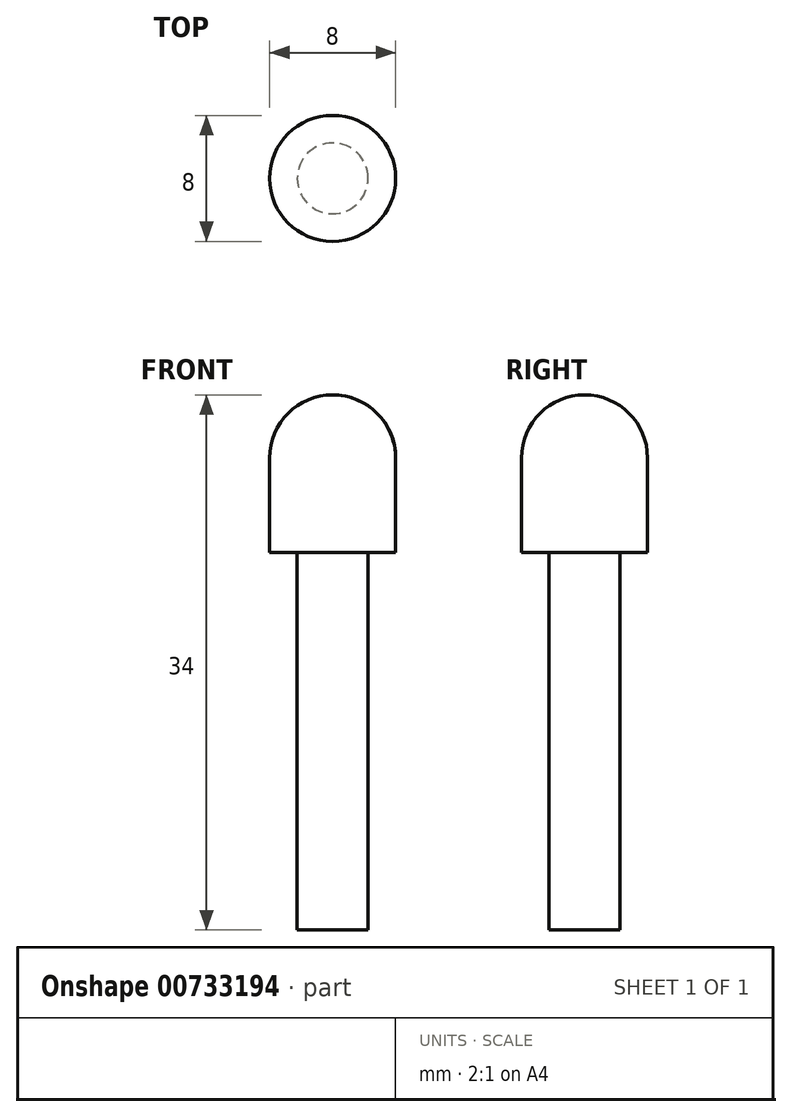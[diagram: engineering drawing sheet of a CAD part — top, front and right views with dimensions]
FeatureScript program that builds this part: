
annotation { "Feature Type Name" : "Feature", "Feature Type Description" : "" }
export const myFeature = defineFeature(function(context is Context, id is Id, definition is map)
    precondition{}
    {
        {
            var Q0;
            Q0=qCreatedBy(makeId("Top.planeOp"),FACE);
            var sketch = newSketch(context, id + "F0", { "sketchPlane" : qUnion([Q0])});
            skCircle(sketch, "E0", {"center": v(0, 0) * mm, "radius": 2.25 * mm});
            skSolve(sketch);
        }
        {
            var Q0;
            Q0=makeQuery(id+"F0.imprint","IMPRINT",FACE,{"disambiguationData":[TD([[makeQuery(id+"F0.imprint","IMPRINT",EDGE,{"derivedFrom":sQuery(id+"F0.wireOp",EDGE,"E0")}),1.0]])]});
            extrude(context, id + "F1", {"entities" : qUnion([Q0]), "depth" : 24 * mm, "offsetDistance" : 25 * mm});
        }
        {
            var Q0;
            Q0=makeQuery(id+"F1.opExtrude","CAP_FACE",FACE,{"disambiguationData":[OSD([sQuery(id+"F0.wireOp",EDGE,"E0")])],"isStart":false});
            var sketch = newSketch(context, id + "F2", { "sketchPlane" : qUnion([Q0])});
            skCircle(sketch, "E1", {"center": v(0, 0) * mm, "radius": 4 * mm});
            skSolve(sketch);
        }
        {
            var Q0;
            Q0=makeQuery(id+"F2.imprint","IMPRINT",FACE,{"disambiguationData":[TD([[makeQuery(id+"F2.imprint","IMPRINT",EDGE,{"derivedFrom":sQuery(id+"F2.wireOp",EDGE,"E1")}),1.0]])]});
            var Q1;
            Q1=makeQuery(id+"F2.imprint","IMPRINT",FACE,{"disambiguationData":[TD([[makeQuery(id+"F2.imprint","IMPRINT",EDGE,{"derivedFrom":makeQuery(id+"F1.opExtrude","CAP_EDGE",EDGE,{"disambiguationData":[OSD([sQuery(id+"F0.wireOp",EDGE,"E0")])],"isStart":false})}),1.0]])]});
            extrude(context, id + "F3", {"entities" : qUnion([Q0, Q1]), "operationType" : NewBodyOperationType.ADD, "depth" : 10 * mm, "offsetDistance" : 25 * mm});
        }
        {
            var Q0;
            Q0=makeQuery(id+"F3.opExtrude","CAP_EDGE",EDGE,{"disambiguationData":[OSD([sQuery(id+"F2.wireOp",EDGE,"E1")])],"isStart":false});
            fillet(context, id + "F4", {"entities" : qUnion([Q0]), "radius" : 4 * mm, "tangentPropagation" : true, "allowEdgeOverflow" : false});
        }
    });
